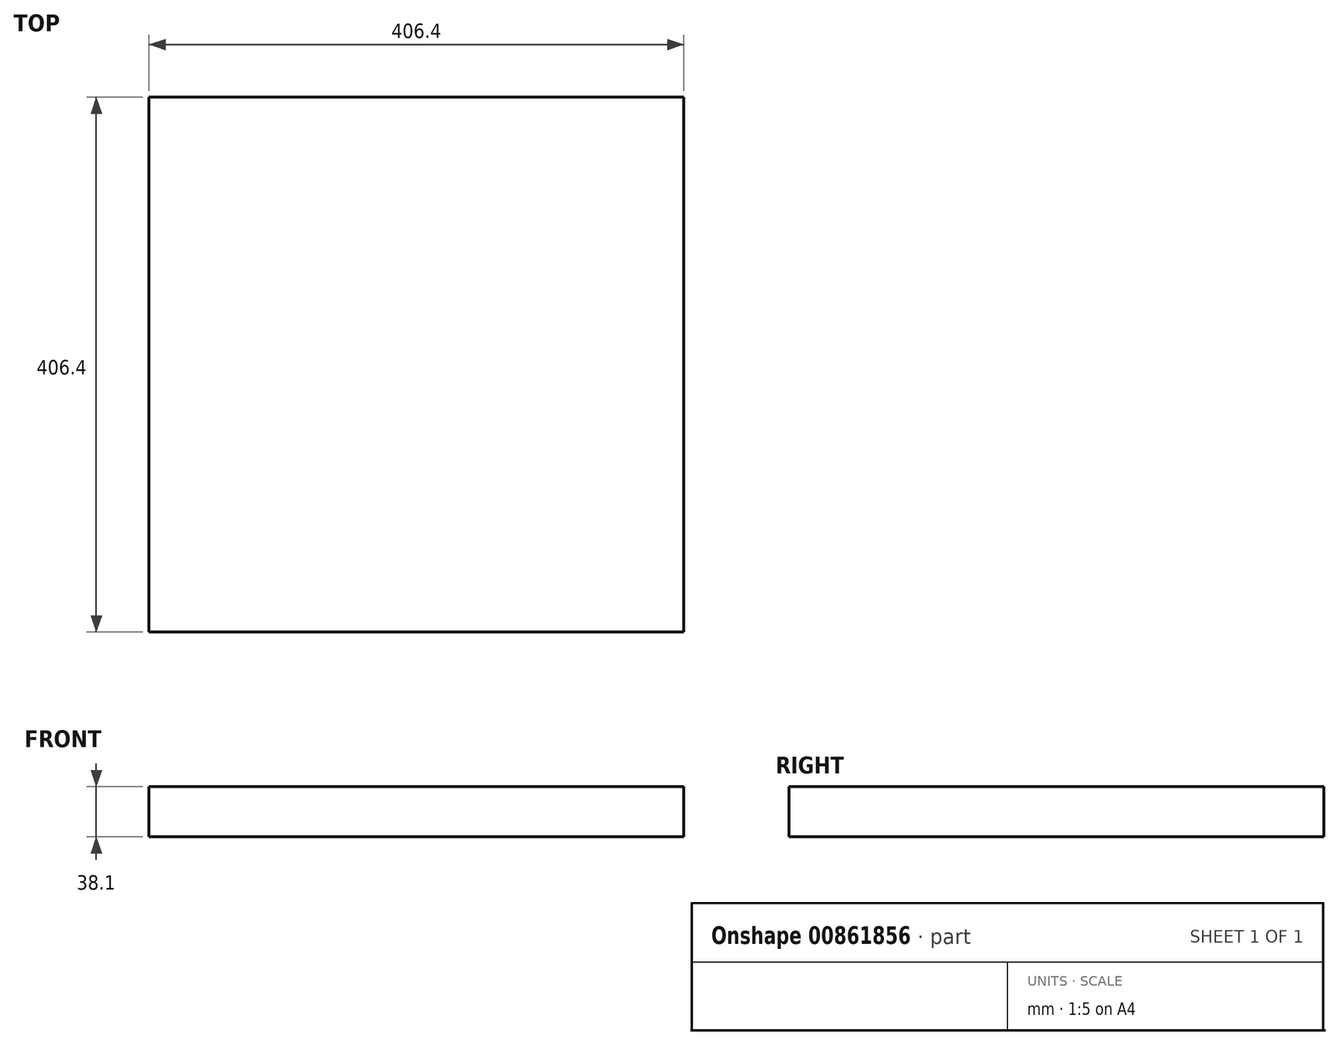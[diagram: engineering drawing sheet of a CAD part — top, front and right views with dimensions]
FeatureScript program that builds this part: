
annotation { "Feature Type Name" : "Feature", "Feature Type Description" : "" }
export const myFeature = defineFeature(function(context is Context, id is Id, definition is map)
    precondition{}
    {
        {
            var Q0;
            Q0=qCreatedBy(makeId("Top.planeOp"),FACE);
            var sketch = newSketch(context, id + "F0", { "sketchPlane" : qUnion([Q0])});
            skLineSegment(sketch, "E0.bottom", {"start": v(203.2, 203.2) * mm, "end": v(-203.2, 203.2) * mm});
            skLineSegment(sketch, "E0.top", {"start": v(203.2, -203.2) * mm, "end": v(-203.2, -203.2) * mm});
            skLineSegment(sketch, "E0.left", {"start": v(203.2, 203.2) * mm, "end": v(203.2, -203.2) * mm});
            skLineSegment(sketch, "E0.right", {"start": v(-203.2, 203.2) * mm, "end": v(-203.2, -203.2) * mm});
            skPoint(sketch, "E0.middle", {"position": v(0, 0) * mm});
            skLineSegment(sketch, "E1", {"start": v(-203.2, 203.2) * mm, "end": v(203.2, -203.2) * mm});
            skLineSegment(sketch, "E2", {"start": v(-203.2, -203.2) * mm, "end": v(203.2, 203.2) * mm});
            skSolve(sketch);
        }
        {
            var Q0;
            {var subQ0=sQuery(id+"F0.wireOp",EDGE,"E0.top");Q0=makeQuery(id+"F0.imprint","IMPRINT",FACE,{"disambiguationData":[TD([[makeQuery(id+"F0.imprint","IMPRINT",EDGE,{"derivedFrom":subQ0}),-1.0]])]});}
            var Q1;
            {var subQ0=sQuery(id+"F0.wireOp",EDGE,"E0.left");Q1=makeQuery(id+"F0.imprint","IMPRINT",FACE,{"disambiguationData":[TD([[makeQuery(id+"F0.imprint","IMPRINT",EDGE,{"derivedFrom":subQ0}),-1.0]])]});}
            var Q2;
            {var subQ0=sQuery(id+"F0.wireOp",EDGE,"E0.right");Q2=makeQuery(id+"F0.imprint","IMPRINT",FACE,{"disambiguationData":[TD([[makeQuery(id+"F0.imprint","IMPRINT",EDGE,{"derivedFrom":subQ0}),1.0]])]});}
            var Q3;
            {var subQ0=sQuery(id+"F0.wireOp",EDGE,"E0.bottom");Q3=makeQuery(id+"F0.imprint","IMPRINT",FACE,{"disambiguationData":[TD([[makeQuery(id+"F0.imprint","IMPRINT",EDGE,{"derivedFrom":subQ0}),1.0]])]});}
            extrude(context, id + "F1", {"entities" : qUnion([Q0, Q1, Q2, Q3]), "depth" : 38.1 * mm, "offsetDistance" : 25.4 * mm});
        }
    });
